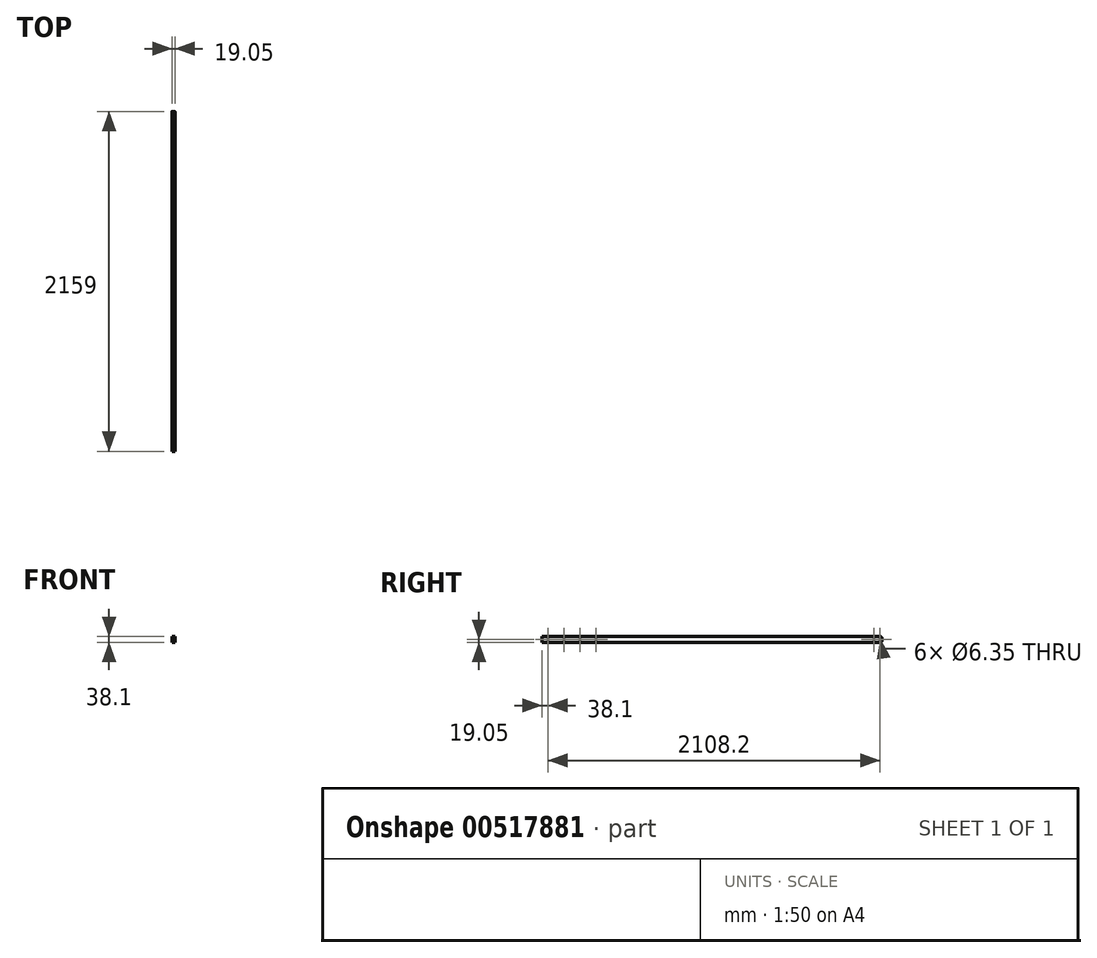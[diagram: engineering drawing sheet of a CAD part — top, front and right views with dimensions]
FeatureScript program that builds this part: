
annotation { "Feature Type Name" : "Feature", "Feature Type Description" : "" }
export const myFeature = defineFeature(function(context is Context, id is Id, definition is map)
    precondition{}
    {
        {
            var Q0;
            Q0=qCreatedBy(makeId("Front.planeOp"),FACE);
            var sketch = newSketch(context, id + "F0", { "sketchPlane" : qUnion([Q0])});
            skLineSegment(sketch, "E0.bottom", {"start": v(0, 0) * mm, "end": v(19.05, 0) * mm});
            skLineSegment(sketch, "E0.top", {"start": v(0, 38.1) * mm, "end": v(19.05, 38.1) * mm});
            skLineSegment(sketch, "E0.left", {"start": v(0, 0) * mm, "end": v(0, 38.1) * mm});
            skLineSegment(sketch, "E0.right", {"start": v(19.05, 0) * mm, "end": v(19.05, 38.1) * mm});
            skLineSegment(sketch, "E1.0", {"start": v(3.17, 34.92) * mm, "end": v(15.87, 34.92) * mm, "construction": true});
            skLineSegment(sketch, "E1.1", {"start": v(3.18, 3.18) * mm, "end": v(3.17, 34.92) * mm, "construction": true});
            skLineSegment(sketch, "E1.2", {"start": v(3.18, 3.18) * mm, "end": v(15.88, 3.18) * mm, "construction": true});
            skLineSegment(sketch, "E1.3", {"start": v(15.88, 3.17) * mm, "end": v(15.87, 34.93) * mm, "construction": true});
            skSolve(sketch);
        }
        {
            var Q0;
            Q0=makeQuery(id+"F0.imprint","IMPRINT",FACE,{"disambiguationData":[TD([[makeQuery(id+"F0.imprint","IMPRINT",EDGE,{"derivedFrom":sQuery(id+"F0.wireOp",EDGE,"E0.bottom")}),1.0]])]});
            extrude(context, id + "F1", {"entities" : qUnion([Q0]), "oppositeDirection" : true, "depth" : 2159 * mm, "offsetDistance" : 25.4 * mm});
        }
        {
            var Q0;
            Q0=makeQuery(id+"F1.opExtrude","SWEPT_FACE",FACE,{"disambiguationData":[OSD([sQuery(id+"F0.wireOp",EDGE,"E0.right")])]});
            var sketch = newSketch(context, id + "F2", { "sketchPlane" : qUnion([Q0])});
            skCircle(sketch, "E2", {"center": v(0, 19.05) * mm, "radius": 3.18 * mm, "construction": true});
            skCircle(sketch, "E3.1.0.0", {"center": v(38.1, 19.05) * mm, "radius": 3.18 * mm});
            skLineSegment(sketch, "E3.direction1", {"start": v(0, 19.05) * mm, "end": v(38.1, 19.05) * mm, "construction": true});
            skCircle(sketch, "E4.1.0.0", {"center": v(2146.3, 19.05) * mm, "radius": 3.18 * mm});
            skLineSegment(sketch, "E4.direction1", {"start": v(38.1, 19.05) * mm, "end": v(2146.3, 19.05) * mm, "construction": true});
            skCircle(sketch, "E5.1.0.0", {"center": v(2108.2, 19.05) * mm, "radius": 3.18 * mm});
            skLineSegment(sketch, "E5.direction1", {"start": v(2146.3, 19.05) * mm, "end": v(2108.2, 19.05) * mm, "construction": true});
            skLineSegment(sketch, "E6.direction1", {"start": v(2108.2, 19.05) * mm, "end": v(1803.4, 19.05) * mm, "construction": true});
            skCircle(sketch, "E7.1.0.0", {"center": v(139.7, 19.05) * mm, "radius": 3.18 * mm});
            skLineSegment(sketch, "E7.direction1", {"start": v(38.1, 19.05) * mm, "end": v(139.7, 19.05) * mm, "construction": true});
            skCircle(sketch, "E8.0.2.0", {"center": v(241.3, 19.05) * mm, "radius": 3.18 * mm});
            skCircle(sketch, "E8.0.3.0", {"center": v(342.9, 19.05) * mm, "radius": 3.18 * mm});
            skSolve(sketch);
        }
        {
            var Q0;
            Q0 = qSketchRegion(id + "F2", true);
            extrude(context, id + "F3", {"entities" : qUnion([Q0]), "operationType" : NewBodyOperationType.REMOVE, "endBound" : BoundingType.THROUGH_ALL, "oppositeDirection" : true, "depth" : 25.4 * mm, "offsetDistance" : 25.4 * mm});
        }
        {
            var Q0;
            Q0=makeQuery(id+"F1.opExtrude","CAP_EDGE",EDGE,{"disambiguationData":[OSD([sQuery(id+"F0.wireOp",EDGE,"E0.top")])],"isStart":false});
            var Q1;
            Q1=makeQuery(id+"F1.opExtrude","CAP_EDGE",EDGE,{"disambiguationData":[OSD([sQuery(id+"F0.wireOp",EDGE,"E0.bottom")])],"isStart":false});
            fillet(context, id + "F4", {"entities" : qUnion([Q0, Q1]), "radius" : 12.7 * mm, "tangentPropagation" : true, "allowEdgeOverflow" : false});
        }
    });
